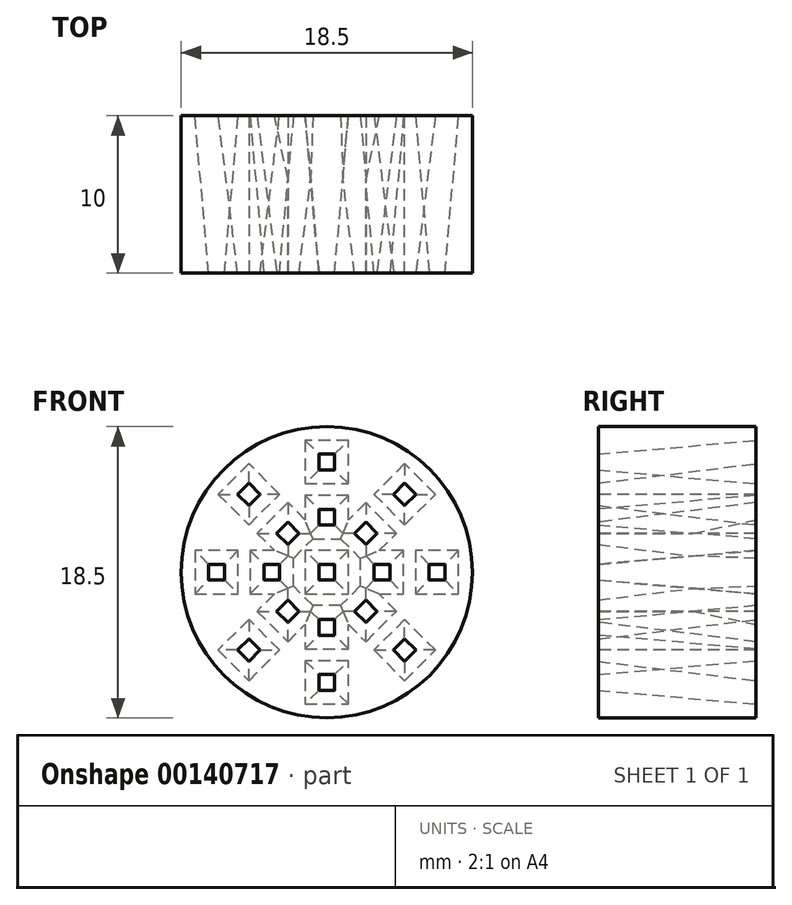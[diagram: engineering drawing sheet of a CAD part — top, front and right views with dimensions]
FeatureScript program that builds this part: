
annotation { "Feature Type Name" : "Feature", "Feature Type Description" : "" }
export const myFeature = defineFeature(function(context is Context, id is Id, definition is map)
    precondition{}
    {
        {
            var Q0;
            Q0=qCreatedBy(makeId("Front.planeOp"),FACE);
            var sketch = newSketch(context, id + "F0", { "sketchPlane" : qUnion([Q0])});
            skCircle(sketch, "E0", {"center": v(0, 0) * mm, "radius": 9.25 * mm});
            skSolve(sketch);
        }
        {
            var Q0;
            Q0 = qSketchRegion(id + "F0", true);
            extrude(context, id + "F1", {"entities" : qUnion([Q0]), "depth" : 10 * mm});
        }
        {
            var Q0;
            Q0=makeQuery(id+"F1.opExtrude","CAP_FACE",FACE,{"disambiguationData":[OSD([sQuery(id+"F0.wireOp",EDGE,"E0")])],"isStart":false});
            var sketch = newSketch(context, id + "F2", { "sketchPlane" : qUnion([Q0])});
            skLineSegment(sketch, "E1.bottom", {"start": v(0.5, -0.5) * mm, "end": v(-0.5, -0.5) * mm});
            skLineSegment(sketch, "E1.top", {"start": v(0.5, 0.5) * mm, "end": v(-0.5, 0.5) * mm});
            skLineSegment(sketch, "E1.left", {"start": v(0.5, -0.5) * mm, "end": v(0.5, 0.5) * mm});
            skLineSegment(sketch, "E1.right", {"start": v(-0.5, -0.5) * mm, "end": v(-0.5, 0.5) * mm});
            skLineSegment(sketch, "E2.1.0.0", {"start": v(4, -0.5) * mm, "end": v(4, 0.5) * mm});
            skLineSegment(sketch, "E2.1.0.1", {"start": v(4, 0.5) * mm, "end": v(3, 0.5) * mm});
            skLineSegment(sketch, "E2.1.0.2", {"start": v(4, -0.5) * mm, "end": v(3, -0.5) * mm});
            skLineSegment(sketch, "E2.1.0.3", {"start": v(3, -0.5) * mm, "end": v(3, 0.5) * mm});
            skLineSegment(sketch, "E2.2.0.0", {"start": v(7.5, -0.5) * mm, "end": v(7.5, 0.5) * mm});
            skLineSegment(sketch, "E2.2.0.1", {"start": v(7.5, 0.5) * mm, "end": v(6.5, 0.5) * mm});
            skLineSegment(sketch, "E2.2.0.2", {"start": v(7.5, -0.5) * mm, "end": v(6.5, -0.5) * mm});
            skLineSegment(sketch, "E2.2.0.3", {"start": v(6.5, -0.5) * mm, "end": v(6.5, 0.5) * mm});
            skLineSegment(sketch, "E2.direction1", {"start": v(0.5, -0.5) * mm, "end": v(4, -0.5) * mm, "construction": true});
            skLineSegment(sketch, "E3.1.0", {"start": v(2.47, 1.77) * mm, "end": v(1.77, 2.47) * mm});
            skLineSegment(sketch, "E3.1.1", {"start": v(2.47, 3.18) * mm, "end": v(1.77, 2.47) * mm});
            skLineSegment(sketch, "E3.1.2", {"start": v(3.18, 2.47) * mm, "end": v(2.47, 3.18) * mm});
            skLineSegment(sketch, "E3.1.3", {"start": v(0.7, 0) * mm, "end": v(3.18, 2.47) * mm, "construction": true});
            skLineSegment(sketch, "E3.1.4", {"start": v(5.66, 4.95) * mm, "end": v(4.95, 4.24) * mm});
            skLineSegment(sketch, "E3.1.5", {"start": v(4.95, 4.24) * mm, "end": v(4.24, 4.95) * mm});
            skLineSegment(sketch, "E3.1.6", {"start": v(4.95, 5.66) * mm, "end": v(4.24, 4.95) * mm});
            skLineSegment(sketch, "E3.1.7", {"start": v(5.66, 4.95) * mm, "end": v(4.95, 5.66) * mm});
            skLineSegment(sketch, "E3.2.0", {"start": v(0.5, 3) * mm, "end": v(-0.5, 3) * mm});
            skLineSegment(sketch, "E3.2.1", {"start": v(-0.5, 4) * mm, "end": v(-0.5, 3) * mm});
            skLineSegment(sketch, "E3.2.2", {"start": v(0.5, 4) * mm, "end": v(-0.5, 4) * mm});
            skLineSegment(sketch, "E3.2.3", {"start": v(0.5, 0.5) * mm, "end": v(0.5, 4) * mm, "construction": true});
            skLineSegment(sketch, "E3.2.4", {"start": v(0.5, 7.5) * mm, "end": v(0.5, 6.5) * mm});
            skLineSegment(sketch, "E3.2.5", {"start": v(0.5, 6.5) * mm, "end": v(-0.5, 6.5) * mm});
            skLineSegment(sketch, "E3.2.6", {"start": v(-0.5, 7.5) * mm, "end": v(-0.5, 6.5) * mm});
            skLineSegment(sketch, "E3.2.7", {"start": v(0.5, 7.5) * mm, "end": v(-0.5, 7.5) * mm});
            skLineSegment(sketch, "E3.3.0", {"start": v(-1.77, 2.47) * mm, "end": v(-2.47, 1.77) * mm});
            skLineSegment(sketch, "E3.3.1", {"start": v(-3.18, 2.47) * mm, "end": v(-2.47, 1.77) * mm});
            skLineSegment(sketch, "E3.3.2", {"start": v(-2.47, 3.18) * mm, "end": v(-3.18, 2.47) * mm});
            skLineSegment(sketch, "E3.3.3", {"start": v(0, 0.7) * mm, "end": v(-2.47, 3.18) * mm, "construction": true});
            skLineSegment(sketch, "E3.3.4", {"start": v(-4.95, 5.66) * mm, "end": v(-4.24, 4.95) * mm});
            skLineSegment(sketch, "E3.3.5", {"start": v(-4.24, 4.95) * mm, "end": v(-4.95, 4.24) * mm});
            skLineSegment(sketch, "E3.3.6", {"start": v(-5.66, 4.95) * mm, "end": v(-4.95, 4.24) * mm});
            skLineSegment(sketch, "E3.3.7", {"start": v(-4.95, 5.66) * mm, "end": v(-5.66, 4.95) * mm});
            skLineSegment(sketch, "E3.4.0", {"start": v(-3, 0.5) * mm, "end": v(-3, -0.5) * mm});
            skLineSegment(sketch, "E3.4.1", {"start": v(-4, -0.5) * mm, "end": v(-3, -0.5) * mm});
            skLineSegment(sketch, "E3.4.2", {"start": v(-4, 0.5) * mm, "end": v(-4, -0.5) * mm});
            skLineSegment(sketch, "E3.4.3", {"start": v(-0.5, 0.5) * mm, "end": v(-4, 0.5) * mm, "construction": true});
            skLineSegment(sketch, "E3.4.4", {"start": v(-7.5, 0.5) * mm, "end": v(-6.5, 0.5) * mm});
            skLineSegment(sketch, "E3.4.5", {"start": v(-6.5, 0.5) * mm, "end": v(-6.5, -0.5) * mm});
            skLineSegment(sketch, "E3.4.6", {"start": v(-7.5, -0.5) * mm, "end": v(-6.5, -0.5) * mm});
            skLineSegment(sketch, "E3.4.7", {"start": v(-7.5, 0.5) * mm, "end": v(-7.5, -0.5) * mm});
            skLineSegment(sketch, "E3.5.0", {"start": v(-2.47, -1.77) * mm, "end": v(-1.77, -2.47) * mm});
            skLineSegment(sketch, "E3.5.1", {"start": v(-2.47, -3.18) * mm, "end": v(-1.77, -2.47) * mm});
            skLineSegment(sketch, "E3.5.2", {"start": v(-3.18, -2.47) * mm, "end": v(-2.47, -3.18) * mm});
            skLineSegment(sketch, "E3.5.3", {"start": v(-0.7, 0) * mm, "end": v(-3.18, -2.47) * mm, "construction": true});
            skLineSegment(sketch, "E3.5.4", {"start": v(-5.66, -4.95) * mm, "end": v(-4.95, -4.24) * mm});
            skLineSegment(sketch, "E3.5.5", {"start": v(-4.95, -4.24) * mm, "end": v(-4.24, -4.95) * mm});
            skLineSegment(sketch, "E3.5.6", {"start": v(-4.95, -5.66) * mm, "end": v(-4.24, -4.95) * mm});
            skLineSegment(sketch, "E3.5.7", {"start": v(-5.66, -4.95) * mm, "end": v(-4.95, -5.66) * mm});
            skLineSegment(sketch, "E3.6.0", {"start": v(-0.5, -3) * mm, "end": v(0.5, -3) * mm});
            skLineSegment(sketch, "E3.6.1", {"start": v(0.5, -4) * mm, "end": v(0.5, -3) * mm});
            skLineSegment(sketch, "E3.6.2", {"start": v(-0.5, -4) * mm, "end": v(0.5, -4) * mm});
            skLineSegment(sketch, "E3.6.3", {"start": v(-0.5, -0.5) * mm, "end": v(-0.5, -4) * mm, "construction": true});
            skLineSegment(sketch, "E3.6.4", {"start": v(-0.5, -7.5) * mm, "end": v(-0.5, -6.5) * mm});
            skLineSegment(sketch, "E3.6.5", {"start": v(-0.5, -6.5) * mm, "end": v(0.5, -6.5) * mm});
            skLineSegment(sketch, "E3.6.6", {"start": v(0.5, -7.5) * mm, "end": v(0.5, -6.5) * mm});
            skLineSegment(sketch, "E3.6.7", {"start": v(-0.5, -7.5) * mm, "end": v(0.5, -7.5) * mm});
            skLineSegment(sketch, "E3.7.0", {"start": v(1.77, -2.47) * mm, "end": v(2.47, -1.77) * mm});
            skLineSegment(sketch, "E3.7.1", {"start": v(3.18, -2.47) * mm, "end": v(2.47, -1.77) * mm});
            skLineSegment(sketch, "E3.7.2", {"start": v(2.47, -3.18) * mm, "end": v(3.18, -2.47) * mm});
            skLineSegment(sketch, "E3.7.3", {"start": v(0, -0.7) * mm, "end": v(2.47, -3.18) * mm, "construction": true});
            skLineSegment(sketch, "E3.7.4", {"start": v(4.95, -5.66) * mm, "end": v(4.24, -4.95) * mm});
            skLineSegment(sketch, "E3.7.5", {"start": v(4.24, -4.95) * mm, "end": v(4.95, -4.24) * mm});
            skLineSegment(sketch, "E3.7.6", {"start": v(5.66, -4.95) * mm, "end": v(4.95, -4.24) * mm});
            skLineSegment(sketch, "E3.7.7", {"start": v(4.95, -5.66) * mm, "end": v(5.66, -4.95) * mm});
            skPoint(sketch, "E3.center", {"position": v(0, 0) * mm});
            skLineSegment(sketch, "E4", {"start": v(1.77, -2.47) * mm, "end": v(2.47, -3.18) * mm});
            skLineSegment(sketch, "E5", {"start": v(-0.5, -3) * mm, "end": v(-0.5, -4) * mm});
            skLineSegment(sketch, "E6", {"start": v(-2.47, -1.77) * mm, "end": v(-3.18, -2.47) * mm});
            skLineSegment(sketch, "E7", {"start": v(-3, 0.5) * mm, "end": v(-4, 0.5) * mm});
            skLineSegment(sketch, "E8", {"start": v(-1.77, 2.47) * mm, "end": v(-2.47, 3.18) * mm});
            skLineSegment(sketch, "E9", {"start": v(0.5, 3) * mm, "end": v(0.5, 4) * mm});
            skLineSegment(sketch, "E10", {"start": v(2.47, 1.77) * mm, "end": v(3.18, 2.47) * mm});
            skSolve(sketch);
        }
        {
            var Q0;
            Q0 = qSketchRegion(id + "F2", true);
            extrude(context, id + "F3", {"entities" : qUnion([Q0]), "operationType" : NewBodyOperationType.REMOVE, "oppositeDirection" : true, "depth" : 25 * mm, "hasDraft" : true, "draftAngle" : 5 * degree});
        }
    });
